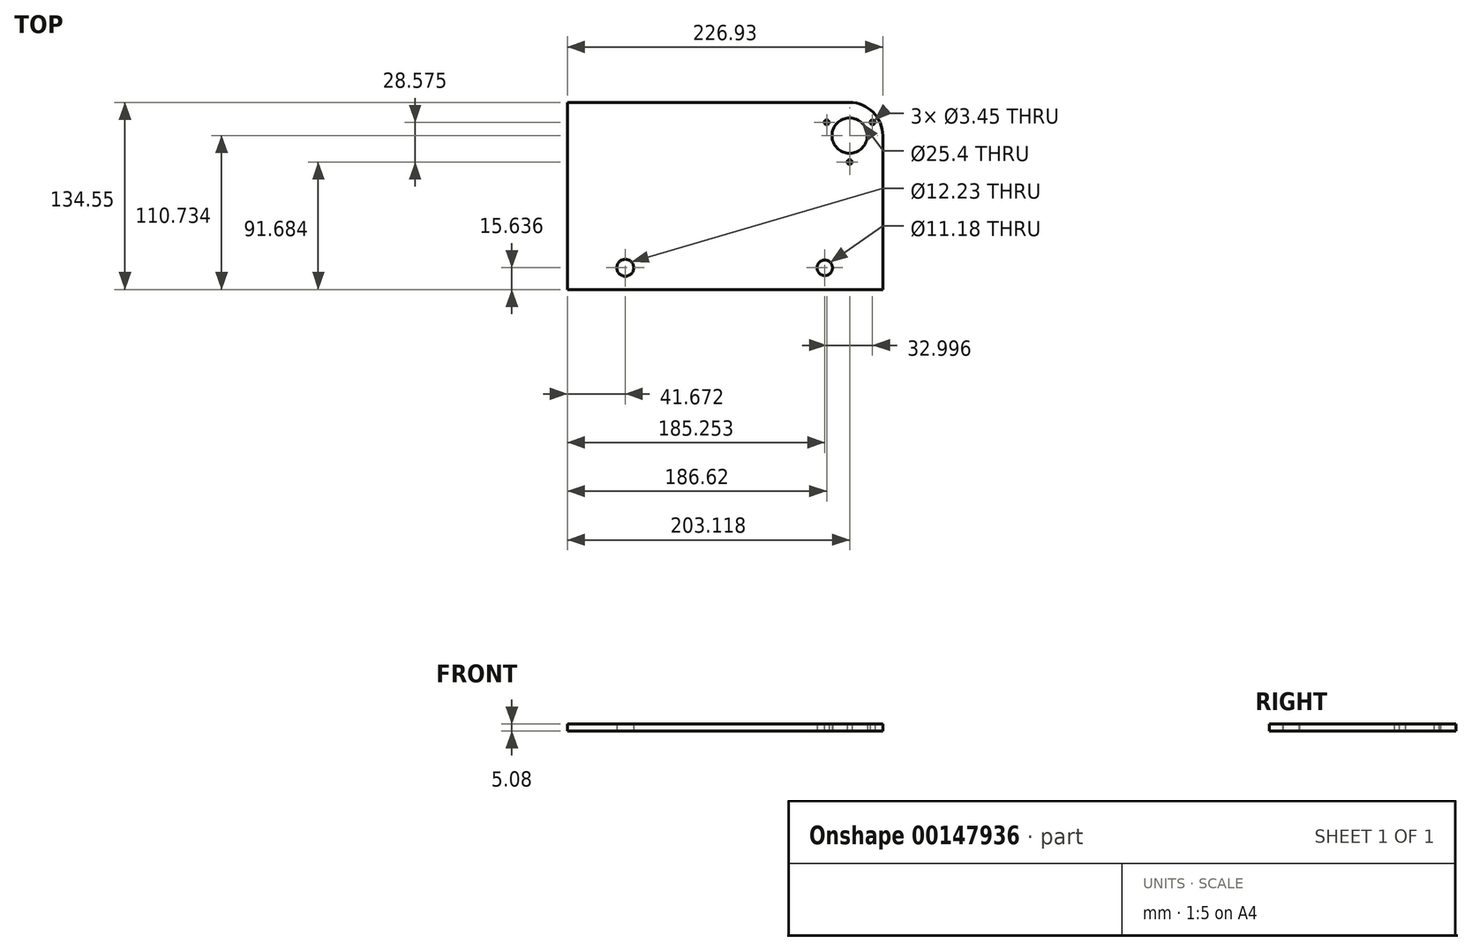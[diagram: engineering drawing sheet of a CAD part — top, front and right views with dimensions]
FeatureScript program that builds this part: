
annotation { "Feature Type Name" : "Feature", "Feature Type Description" : "" }
export const myFeature = defineFeature(function(context is Context, id is Id, definition is map)
    precondition{}
    {
        {
            var Q0;
            Q0=qCreatedBy(makeId("Top.planeOp"),FACE);
            var sketch = newSketch(context, id + "F0", { "sketchPlane" : qUnion([Q0])});
            skCircle(sketch, "E0", {"center": v(-23.81, 110.73) * mm, "radius": 12.7 * mm});
            skCircle(sketch, "E1.cCircle", {"center": v(-23.81, 110.73) * mm, "radius": 9.52 * mm, "construction": true});
            skLineSegment(sketch, "E1.0", {"start": v(-40.31, 120.26) * mm, "end": v(-7.31, 120.26) * mm, "construction": true});
            skLineSegment(sketch, "E1.1", {"start": v(-7.31, 120.26) * mm, "end": v(-23.81, 91.68) * mm, "construction": true});
            skLineSegment(sketch, "E1.2", {"start": v(-23.81, 91.68) * mm, "end": v(-40.31, 120.26) * mm, "construction": true});
            skPoint(sketch, "E1.0.midPoint", {"position": v(-23.81, 120.26) * mm});
            skCircle(sketch, "E2", {"center": v(-23.81, 110.73) * mm, "radius": 14.29 * mm, "construction": true});
            skCircle(sketch, "E3", {"center": v(-40.31, 120.26) * mm, "radius": 4.76 * mm, "construction": true});
            skCircle(sketch, "E4", {"center": v(-40.31, 120.26) * mm, "radius": 1.73 * mm});
            skCircle(sketch, "E5", {"center": v(-7.31, 120.26) * mm, "radius": 1.73 * mm});
            skCircle(sketch, "E6", {"center": v(-23.81, 91.68) * mm, "radius": 1.73 * mm});
            skLineSegment(sketch, "E7.bottom", {"start": v(-226.93, 134.55) * mm, "end": v(0, 134.55) * mm});
            skLineSegment(sketch, "E7.top", {"start": v(-226.93, 0) * mm, "end": v(0, 0) * mm});
            skLineSegment(sketch, "E7.left", {"start": v(-226.93, 134.55) * mm, "end": v(-226.93, 0) * mm});
            skLineSegment(sketch, "E7.right", {"start": v(0, 134.55) * mm, "end": v(0, 0) * mm});
            skCircle(sketch, "E8", {"center": v(-23.81, 110.73) * mm, "radius": 23.81 * mm, "construction": true});
            skLineSegment(sketch, "E9", {"start": v(-41.68, 0) * mm, "end": v(-41.68, 15.64) * mm, "construction": true});
            skLineSegment(sketch, "E10", {"start": v(-41.68, 15.64) * mm, "end": v(0, 15.64) * mm, "construction": true});
            skLineSegment(sketch, "E11", {"start": v(-226.93, 15.64) * mm, "end": v(-185.26, 15.64) * mm, "construction": true});
            skCircle(sketch, "E12", {"center": v(-185.26, 15.64) * mm, "radius": 6.11 * mm});
            skCircle(sketch, "E13", {"center": v(-41.68, 15.64) * mm, "radius": 5.59 * mm});
            skSolve(sketch);
        }
        {
            var Q0;
            Q0=qSketchRegion(id+"F0",true);
            extrude(context, id + "F1", {"entities" : qUnion([Q0]), "depth" : 5.08 * mm});
        }
        {
            var Q0;
            Q0=makeQuery(id+"F1.opExtrude","SWEPT_EDGE",EDGE,{"disambiguationData":[OSD([sQuery(id+"F0.wireOp",EDGE,"E7.bottom"),sQuery(id+"F0.wireOp",EDGE,"E7.right")])]});
            fillet(context, id + "F2", {"entities" : qUnion([Q0]), "radius" : 23.8 * mm, "tangentPropagation" : true, "allowEdgeOverflow" : false});
        }
    });
